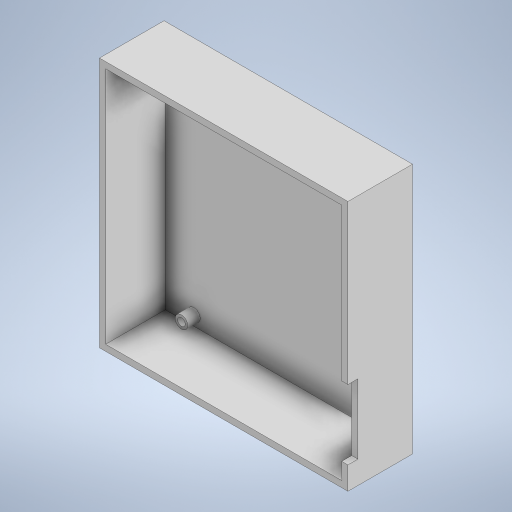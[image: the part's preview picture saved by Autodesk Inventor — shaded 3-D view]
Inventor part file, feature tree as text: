
AUTODESK INVENTOR PART (.ipt)
format: ipt  version: 2023 (Build 270158000, 158)  size: 251,904 bytes
history: native  units: mm
features: extrude x4, sketch x4, other x1
ambient origin geometry x8: Origin, YZ Plane, XZ Plane, XY Plane, X Axis, Y Axis, Z Axis, Center Point
bodies: Body1 (feature_tree)
feature tree (9):
  other  "Sólido1"
  extrude  "Base"  Depth=101.0mm
  extrude  "Área"  Depth=2.5mm
  extrude  "Extrusão3"  Depth=24.0mm
  extrude  "Extrusão4"  Depth=28.0mm
  sketch  "Esboço1"  dims[d0=100.0mm d1=101.0mm]
  sketch  "Esboço2"  dims[d2=26.0mm d3=0.0mm d4=2.5mm]
  sketch  "Esboço3"  dims[d5=24.0mm d6=0.0mm d11=3.0mm]
  sketch  "Esboço4"  dims[d12=14.0mm d13=6.5mm d14=5.0mm d15=5.0mm d16=0.0mm d17=4.0mm d18=28.0mm d19=0.0mm d20=0.0mm]
